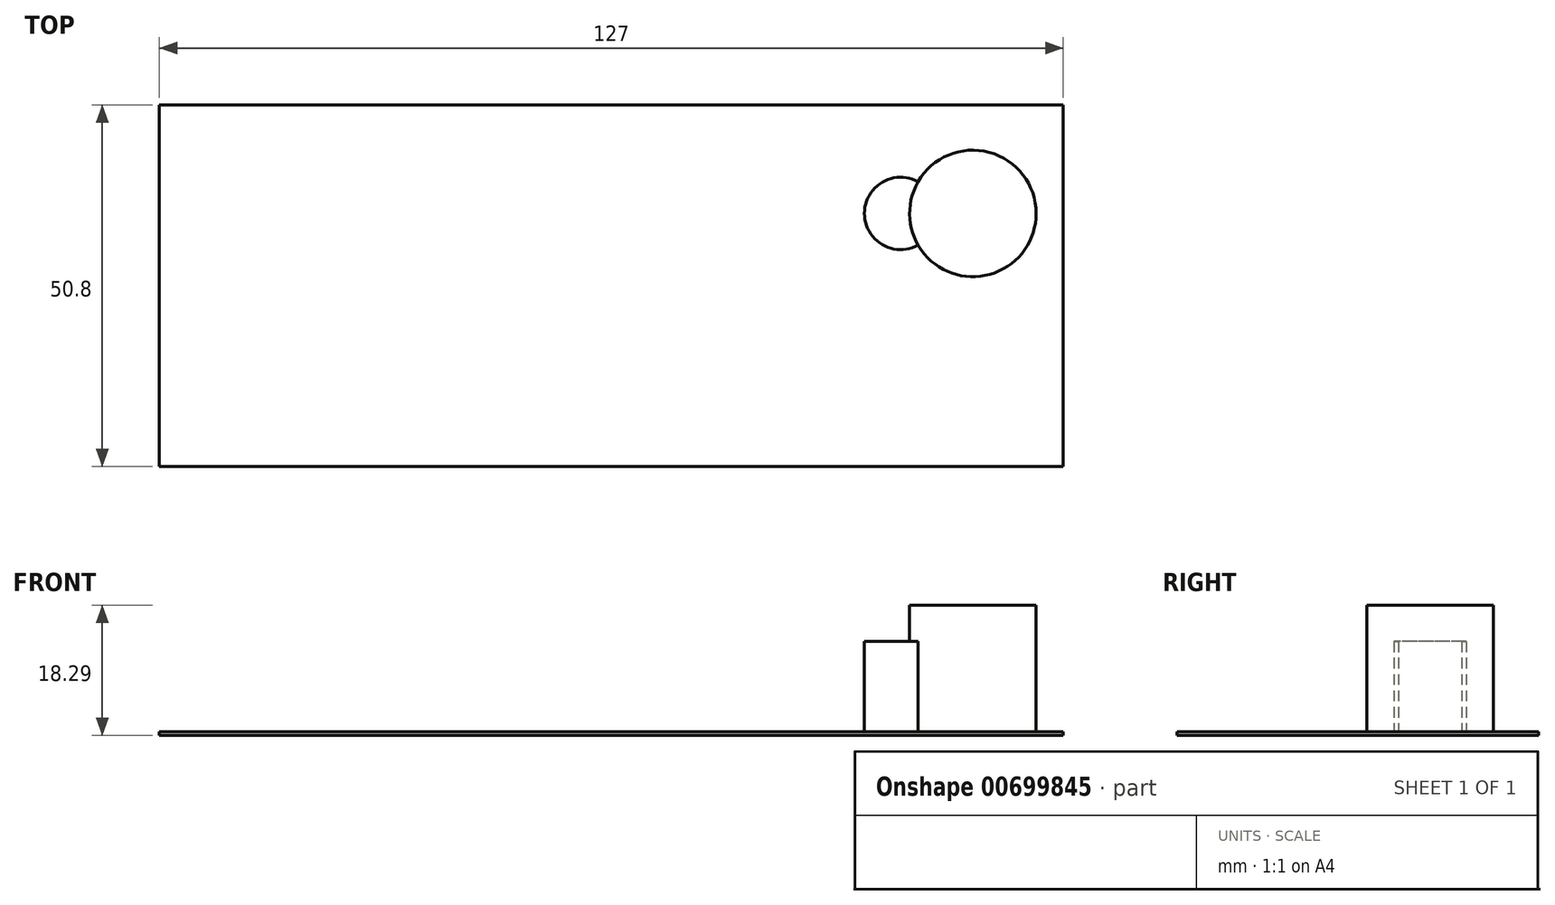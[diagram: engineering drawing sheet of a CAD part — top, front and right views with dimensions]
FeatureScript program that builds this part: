
annotation { "Feature Type Name" : "Feature", "Feature Type Description" : "" }
export const myFeature = defineFeature(function(context is Context, id is Id, definition is map)
    precondition{}
    {
        {
            var Q0;
            Q0=qCreatedBy(makeId("Top.planeOp"),FACE);
            var sketch = newSketch(context, id + "F0", { "sketchPlane" : qUnion([Q0])});
            skLineSegment(sketch, "E0.bottom", {"start": v(-127, 0) * mm, "end": v(0, 0) * mm});
            skLineSegment(sketch, "E0.top", {"start": v(-127, -50.8) * mm, "end": v(0, -50.8) * mm});
            skLineSegment(sketch, "E0.left", {"start": v(-127, 0) * mm, "end": v(-127, -50.8) * mm});
            skLineSegment(sketch, "E0.right", {"start": v(0, 0) * mm, "end": v(0, -50.8) * mm});
            skSolve(sketch);
        }
        {
            var Q0;
            Q0=makeQuery(id+"F0.imprint","IMPRINT",FACE,{"disambiguationData":[TD([[makeQuery(id+"F0.imprint","IMPRINT",EDGE,{"derivedFrom":sQuery(id+"F0.wireOp",EDGE,"E0.bottom")}),-1.0]])]});
            extrude(context, id + "F1", {"entities" : qUnion([Q0]), "depth" : 0.5 * mm, "offsetDistance" : 25.4 * mm});
        }
        {
            var Q0;
            Q0=makeQuery(id+"F1.opExtrude","CAP_FACE",FACE,{"disambiguationData":[OSD([sQuery(id+"F0.wireOp",EDGE,"E0.bottom"),sQuery(id+"F0.wireOp",EDGE,"E0.top"),sQuery(id+"F0.wireOp",EDGE,"E0.left"),sQuery(id+"F0.wireOp",EDGE,"E0.right")])],"isStart":false});
            var sketch = newSketch(context, id + "F2", { "sketchPlane" : qUnion([Q0])});
            skCircle(sketch, "E1", {"center": v(-12.7, -15.24) * mm, "radius": 8.9 * mm});
            skCircle(sketch, "E2", {"center": v(-22.86, -15.24) * mm, "radius": 5.08 * mm});
            skSolve(sketch);
        }
        {
            var Q0;
            Q0 = qSketchRegion(id + "F2", true);
            extrude(context, id + "F3", {"entities" : qUnion([Q0]), "operationType" : NewBodyOperationType.ADD, "depth" : 12.7 * mm, "offsetDistance" : 25.4 * mm});
        }
        {
            var Q0;
            Q0=makeQuery(id+"F3.opExtrude","CAP_FACE",FACE,{"disambiguationData":[OSD([sQuery(id+"F2.wireOp",EDGE,"E1"),sQuery(id+"F2.wireOp",EDGE,"E2")])],"isStart":false});
            var sketch = newSketch(context, id + "F4", { "sketchPlane" : qUnion([Q0])});
            skCircle(sketch, "E3", {"center": v(-12.7, -15.24) * mm, "radius": 8.9 * mm});
            skPoint(sketch, "E3.first.point", {"position": v(-19.37, -9.37) * mm});
            skPoint(sketch, "E3.second.point", {"position": v(-3.87, -16.27) * mm});
            skPoint(sketch, "E3.third.point", {"position": v(-18.76, -21.74) * mm});
            skSolve(sketch);
        }
        {
            var Q0;
            {var subQ0=sQuery(id+"F4.wireOp",EDGE,"E3");var subQ1=makeQuery(id+"F3.opExtrude","CAP_EDGE",EDGE,{"disambiguationData":[OSD([sQuery(id+"F2.wireOp",EDGE,"E2")])],"isStart":false});var subQ2=makeQuery(id+"F4.imprint","INTERSECT",VERTEX,{"disambiguationData":[OD(0.0)],"derivedFrom":[subQ1,subQ0]});Q0=makeQuery(id+"F4.imprint","IMPRINT",FACE,{"disambiguationData":[TD([[makeQuery(id+"F4.imprint","IMPRINT",EDGE,{"disambiguationData":[TD([[subQ2,1.0]])],"derivedFrom":subQ0}),1.0]])]});}
            extrude(context, id + "F5", {"entities" : qUnion([Q0]), "operationType" : NewBodyOperationType.ADD, "depth" : 5.08 * mm, "offsetDistance" : 25.4 * mm});
        }
    });
